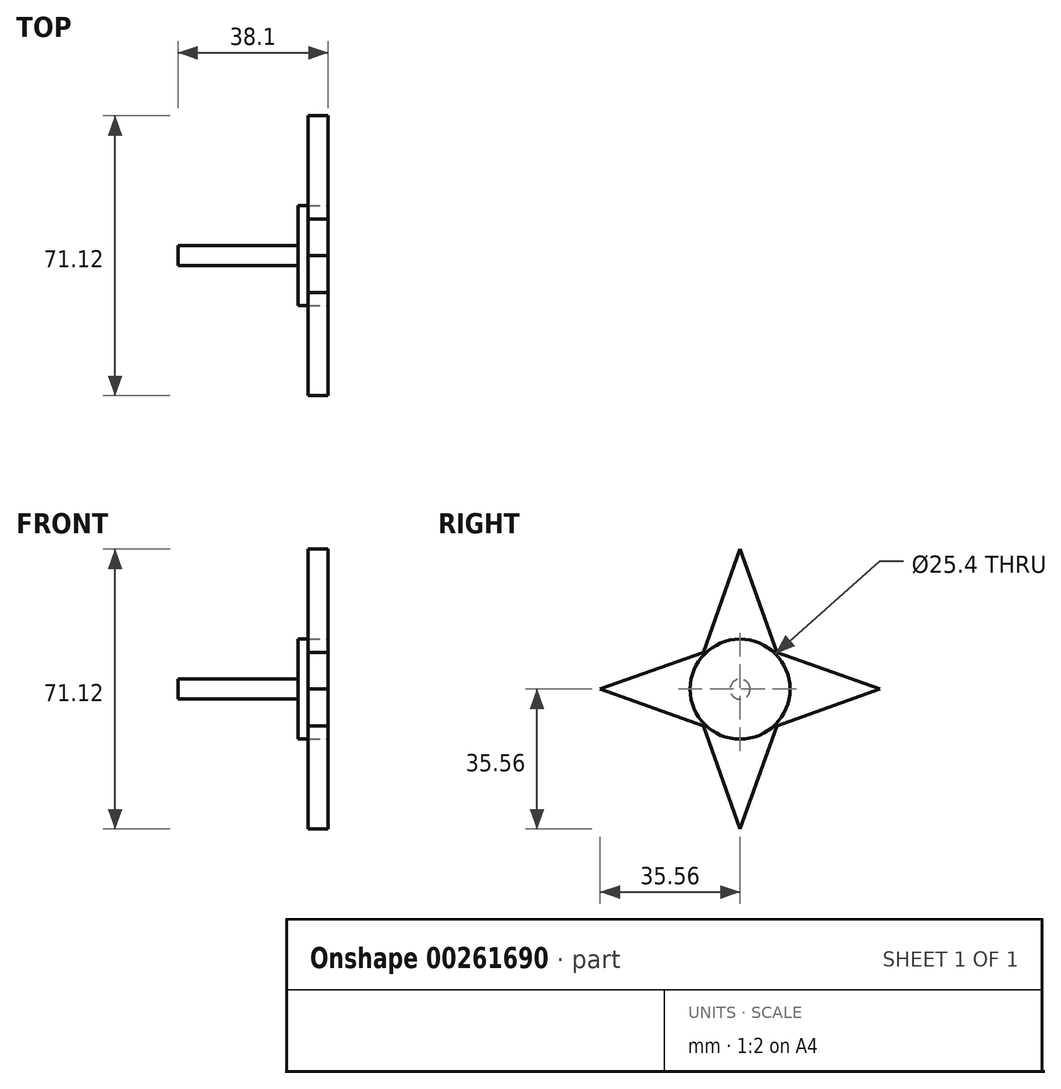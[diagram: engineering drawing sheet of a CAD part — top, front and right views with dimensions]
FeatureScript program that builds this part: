
annotation { "Feature Type Name" : "Feature", "Feature Type Description" : "" }
export const myFeature = defineFeature(function(context is Context, id is Id, definition is map)
    precondition{}
    {
        {
            var Q0;
            Q0=qCreatedBy(makeId("Right.planeOp"),FACE);
            var sketch = newSketch(context, id + "F0", { "sketchPlane" : qUnion([Q0])});
            skLineSegment(sketch, "E0.bottom", {"start": v(0, 0) * mm, "end": v(-71.12, 0) * mm});
            skLineSegment(sketch, "E0.top", {"start": v(0, -71.12) * mm, "end": v(-71.12, -71.12) * mm});
            skLineSegment(sketch, "E0.left", {"start": v(0, 0) * mm, "end": v(0, -71.12) * mm});
            skLineSegment(sketch, "E0.right", {"start": v(-71.12, 0) * mm, "end": v(-71.12, -71.12) * mm});
            skLineSegment(sketch, "E1", {"start": v(-35.56, 0) * mm, "end": v(-35.56, -71.12) * mm});
            skLineSegment(sketch, "E2", {"start": v(0, -35.56) * mm, "end": v(-71.12, -35.56) * mm});
            skLineSegment(sketch, "E3", {"start": v(-35.56, 0) * mm, "end": v(-22.86, -35.56) * mm});
            skLineSegment(sketch, "E4", {"start": v(0, -35.56) * mm, "end": v(-35.56, -22.86) * mm});
            skLineSegment(sketch, "E5", {"start": v(0, -35.56) * mm, "end": v(-35.56, -48.26) * mm});
            skLineSegment(sketch, "E6", {"start": v(-22.86, -35.56) * mm, "end": v(-35.56, -71.12) * mm});
            skLineSegment(sketch, "E7", {"start": v(-35.56, -71.12) * mm, "end": v(-48.26, -35.56) * mm});
            skLineSegment(sketch, "E8", {"start": v(-48.26, -35.56) * mm, "end": v(-35.56, 0) * mm});
            skLineSegment(sketch, "E9", {"start": v(-35.56, -22.86) * mm, "end": v(-71.12, -35.56) * mm});
            skLineSegment(sketch, "E10", {"start": v(-71.12, -35.56) * mm, "end": v(-35.56, -48.26) * mm});
            skCircle(sketch, "E11", {"center": v(-35.56, -35.56) * mm, "radius": 2.54 * mm});
            skCircle(sketch, "E12", {"center": v(-35.56, -35.56) * mm, "radius": 12.7 * mm});
            skSolve(sketch);
        }
        {
            var Q0;
            {var subQ0=sQuery(id+"F0.wireOp",EDGE,"E2");var subQ1=sQuery(id+"F0.wireOp",EDGE,"E1");var subQ2=makeQuery(id+"F0.imprint","INTERSECT",VERTEX,{"derivedFrom":[subQ1,subQ0]});Q0=makeQuery(id+"F0.imprint","IMPRINT",FACE,{"disambiguationData":[TD([[makeQuery(id+"F0.imprint","IMPRINT",EDGE,{"disambiguationData":[TD([[subQ2,-1.0]])],"derivedFrom":subQ1}),-1.0]])]});}
            var Q1;
            {var subQ0=sQuery(id+"F0.wireOp",EDGE,"E11");var subQ1=sQuery(id+"F0.wireOp",EDGE,"E1");var subQ2=makeQuery(id+"F0.imprint","INTERSECT",VERTEX,{"disambiguationData":[OD(0.0)],"derivedFrom":[subQ1,subQ0]});Q1=makeQuery(id+"F0.imprint","IMPRINT",FACE,{"disambiguationData":[TD([[makeQuery(id+"F0.imprint","IMPRINT",EDGE,{"disambiguationData":[TD([[subQ2,-1.0]])],"derivedFrom":subQ1}),-1.0]])]});}
            var Q2;
            {var subQ0=sQuery(id+"F0.wireOp",EDGE,"E11");var subQ1=sQuery(id+"F0.wireOp",EDGE,"E1");var subQ2=makeQuery(id+"F0.imprint","INTERSECT",VERTEX,{"disambiguationData":[OD(0.0)],"derivedFrom":[subQ1,subQ0]});Q2=makeQuery(id+"F0.imprint","IMPRINT",FACE,{"disambiguationData":[TD([[makeQuery(id+"F0.imprint","IMPRINT",EDGE,{"disambiguationData":[TD([[subQ2,-1.0]])],"derivedFrom":subQ1}),1.0]])]});}
            var Q3;
            {var subQ0=sQuery(id+"F0.wireOp",EDGE,"E2");var subQ1=sQuery(id+"F0.wireOp",EDGE,"E1");var subQ2=makeQuery(id+"F0.imprint","INTERSECT",VERTEX,{"derivedFrom":[subQ1,subQ0]});Q3=makeQuery(id+"F0.imprint","IMPRINT",FACE,{"disambiguationData":[TD([[makeQuery(id+"F0.imprint","IMPRINT",EDGE,{"disambiguationData":[TD([[subQ2,-1.0]])],"derivedFrom":subQ1}),1.0]])]});}
            extrude(context, id + "F1", {"entities" : qUnion([Q0, Q1, Q2, Q3]), "oppositeDirection" : true, "depth" : 38.1 * mm});
        }
        {
            var Q0;
            {var subQ1=sQuery(id+"F0.wireOp",EDGE,"E1");var subQ7=sQuery(id+"F0.wireOp",EDGE,"E11");var subQ9=makeQuery(id+"F0.imprint","INTERSECT",VERTEX,{"disambiguationData":[OD(0.0)],"derivedFrom":[subQ1,subQ7]});Q0=makeQuery(id+"F0.imprint","IMPRINT",FACE,{"disambiguationData":[TD([[makeQuery(id+"F0.imprint","IMPRINT",EDGE,{"disambiguationData":[TD([[subQ9,1.0]])],"derivedFrom":subQ7}),-1.0]])]});}
            var Q1;
            {var subQ1=sQuery(id+"F0.wireOp",EDGE,"E1");var subQ7=sQuery(id+"F0.wireOp",EDGE,"E11");var subQ9=makeQuery(id+"F0.imprint","INTERSECT",VERTEX,{"disambiguationData":[OD(0.0)],"derivedFrom":[subQ1,subQ7]});Q1=makeQuery(id+"F0.imprint","IMPRINT",FACE,{"disambiguationData":[TD([[makeQuery(id+"F0.imprint","IMPRINT",EDGE,{"disambiguationData":[TD([[subQ9,-1.0]])],"derivedFrom":subQ7}),-1.0]])]});}
            var Q2;
            {var subQ1=sQuery(id+"F0.wireOp",EDGE,"E1");var subQ7=sQuery(id+"F0.wireOp",EDGE,"E11");var subQ9=makeQuery(id+"F0.imprint","INTERSECT",VERTEX,{"disambiguationData":[OD(1.0)],"derivedFrom":[subQ1,subQ7]});Q2=makeQuery(id+"F0.imprint","IMPRINT",FACE,{"disambiguationData":[TD([[makeQuery(id+"F0.imprint","IMPRINT",EDGE,{"disambiguationData":[TD([[subQ9,1.0]])],"derivedFrom":subQ7}),-1.0]])]});}
            var Q3;
            {var subQ5=sQuery(id+"F0.wireOp",EDGE,"E11");var subQ7=sQuery(id+"F0.wireOp",EDGE,"E1");var subQ9=makeQuery(id+"F0.imprint","INTERSECT",VERTEX,{"disambiguationData":[OD(1.0)],"derivedFrom":[subQ7,subQ5]});Q3=makeQuery(id+"F0.imprint","IMPRINT",FACE,{"disambiguationData":[TD([[makeQuery(id+"F0.imprint","IMPRINT",EDGE,{"disambiguationData":[TD([[subQ9,-1.0]])],"derivedFrom":subQ5}),-1.0]])]});}
            var Q4;
            {var subQ0=sQuery(id+"F0.wireOp",EDGE,"E12");var subQ1=sQuery(id+"F0.wireOp",EDGE,"E8");var subQ3=makeQuery(id+"F0.imprint","INTERSECT",VERTEX,{"derivedFrom":[subQ1,subQ0]});Q4=makeQuery(id+"F0.imprint","IMPRINT",FACE,{"disambiguationData":[TD([[makeQuery(id+"F0.imprint","IMPRINT",EDGE,{"disambiguationData":[TD([[subQ3,1.0]])],"derivedFrom":subQ1}),1.0]])]});}
            var Q5;
            {var subQ0=sQuery(id+"F0.wireOp",EDGE,"E12");var subQ1=sQuery(id+"F0.wireOp",EDGE,"E9");var subQ3=makeQuery(id+"F0.imprint","INTERSECT",VERTEX,{"derivedFrom":[subQ1,subQ0]});Q5=makeQuery(id+"F0.imprint","IMPRINT",FACE,{"disambiguationData":[TD([[makeQuery(id+"F0.imprint","IMPRINT",EDGE,{"disambiguationData":[TD([[subQ3,1.0]])],"derivedFrom":subQ1}),-1.0]])]});}
            var Q6;
            {var subQ0=sQuery(id+"F0.wireOp",EDGE,"E12");var subQ1=sQuery(id+"F0.wireOp",EDGE,"E4");var subQ3=makeQuery(id+"F0.imprint","INTERSECT",VERTEX,{"derivedFrom":[subQ1,subQ0]});Q6=makeQuery(id+"F0.imprint","IMPRINT",FACE,{"disambiguationData":[TD([[makeQuery(id+"F0.imprint","IMPRINT",EDGE,{"disambiguationData":[TD([[subQ3,-1.0]])],"derivedFrom":subQ1}),-1.0]])]});}
            var Q7;
            {var subQ0=sQuery(id+"F0.wireOp",EDGE,"E12");var subQ1=sQuery(id+"F0.wireOp",EDGE,"E3");var subQ3=makeQuery(id+"F0.imprint","INTERSECT",VERTEX,{"derivedFrom":[subQ1,subQ0]});Q7=makeQuery(id+"F0.imprint","IMPRINT",FACE,{"disambiguationData":[TD([[makeQuery(id+"F0.imprint","IMPRINT",EDGE,{"disambiguationData":[TD([[subQ3,-1.0]])],"derivedFrom":subQ1}),1.0]])]});}
            var Q8;
            {var subQ0=sQuery(id+"F0.wireOp",EDGE,"E12");var subQ1=sQuery(id+"F0.wireOp",EDGE,"E6");var subQ3=makeQuery(id+"F0.imprint","INTERSECT",VERTEX,{"derivedFrom":[subQ1,subQ0]});Q8=makeQuery(id+"F0.imprint","IMPRINT",FACE,{"disambiguationData":[TD([[makeQuery(id+"F0.imprint","IMPRINT",EDGE,{"disambiguationData":[TD([[subQ3,1.0]])],"derivedFrom":subQ1}),1.0]])]});}
            var Q9;
            {var subQ0=sQuery(id+"F0.wireOp",EDGE,"E12");var subQ1=sQuery(id+"F0.wireOp",EDGE,"E5");var subQ3=makeQuery(id+"F0.imprint","INTERSECT",VERTEX,{"derivedFrom":[subQ1,subQ0]});Q9=makeQuery(id+"F0.imprint","IMPRINT",FACE,{"disambiguationData":[TD([[makeQuery(id+"F0.imprint","IMPRINT",EDGE,{"disambiguationData":[TD([[subQ3,-1.0]])],"derivedFrom":subQ1}),1.0]])]});}
            var Q10;
            {var subQ0=sQuery(id+"F0.wireOp",EDGE,"E12");var subQ1=sQuery(id+"F0.wireOp",EDGE,"E10");var subQ3=makeQuery(id+"F0.imprint","INTERSECT",VERTEX,{"derivedFrom":[subQ1,subQ0]});Q10=makeQuery(id+"F0.imprint","IMPRINT",FACE,{"disambiguationData":[TD([[makeQuery(id+"F0.imprint","IMPRINT",EDGE,{"disambiguationData":[TD([[subQ3,-1.0]])],"derivedFrom":subQ1}),-1.0]])]});}
            var Q11;
            {var subQ0=sQuery(id+"F0.wireOp",EDGE,"E12");var subQ1=sQuery(id+"F0.wireOp",EDGE,"E7");var subQ3=makeQuery(id+"F0.imprint","INTERSECT",VERTEX,{"derivedFrom":[subQ1,subQ0]});Q11=makeQuery(id+"F0.imprint","IMPRINT",FACE,{"disambiguationData":[TD([[makeQuery(id+"F0.imprint","IMPRINT",EDGE,{"disambiguationData":[TD([[subQ3,-1.0]])],"derivedFrom":subQ1}),1.0]])]});}
            extrude(context, id + "F2", {"entities" : qUnion([Q0, Q1, Q2, Q3, Q4, Q5, Q6, Q7, Q8, Q9, Q10, Q11]), "operationType" : NewBodyOperationType.ADD, "oppositeDirection" : true, "depth" : 7.62 * mm});
        }
        {
            var Q0;
            {var subQ3=sQuery(id+"F0.wireOp",EDGE,"E12");var subQ4=sQuery(id+"F0.wireOp",EDGE,"E8");var subQ6=makeQuery(id+"F0.imprint","INTERSECT",VERTEX,{"derivedFrom":[subQ4,subQ3]});Q0=makeQuery(id+"F0.imprint","IMPRINT",FACE,{"disambiguationData":[TD([[makeQuery(id+"F0.imprint","IMPRINT",EDGE,{"disambiguationData":[TD([[subQ6,-1.0]])],"derivedFrom":subQ4}),1.0]])]});}
            var Q1;
            {var subQ0=sQuery(id+"F0.wireOp",EDGE,"E10");var subQ4=sQuery(id+"F0.wireOp",EDGE,"E7");var subQ7=makeQuery(id+"F0.imprint","INTERSECT",VERTEX,{"derivedFrom":[subQ4,subQ0]});Q1=makeQuery(id+"F0.imprint","IMPRINT",FACE,{"disambiguationData":[TD([[makeQuery(id+"F0.imprint","IMPRINT",EDGE,{"disambiguationData":[TD([[subQ7,-1.0]])],"derivedFrom":subQ4}),1.0]])]});}
            var Q2;
            {var subQ0=sQuery(id+"F0.wireOp",EDGE,"E7");var subQ4=sQuery(id+"F0.wireOp",EDGE,"E10");var subQ6=makeQuery(id+"F0.imprint","INTERSECT",VERTEX,{"derivedFrom":[subQ0,subQ4]});Q2=makeQuery(id+"F0.imprint","IMPRINT",FACE,{"disambiguationData":[TD([[makeQuery(id+"F0.imprint","IMPRINT",EDGE,{"disambiguationData":[TD([[subQ6,-1.0]])],"derivedFrom":subQ4}),-1.0]])]});}
            var Q3;
            {var subQ0=sQuery(id+"F0.wireOp",EDGE,"E6");var subQ4=sQuery(id+"F0.wireOp",EDGE,"E5");var subQ6=makeQuery(id+"F0.imprint","INTERSECT",VERTEX,{"derivedFrom":[subQ4,subQ0]});Q3=makeQuery(id+"F0.imprint","IMPRINT",FACE,{"disambiguationData":[TD([[makeQuery(id+"F0.imprint","IMPRINT",EDGE,{"disambiguationData":[TD([[subQ6,-1.0]])],"derivedFrom":subQ4}),1.0]])]});}
            var Q4;
            {var subQ0=sQuery(id+"F0.wireOp",EDGE,"E5");var subQ4=sQuery(id+"F0.wireOp",EDGE,"E6");var subQ7=makeQuery(id+"F0.imprint","INTERSECT",VERTEX,{"derivedFrom":[subQ0,subQ4]});Q4=makeQuery(id+"F0.imprint","IMPRINT",FACE,{"disambiguationData":[TD([[makeQuery(id+"F0.imprint","IMPRINT",EDGE,{"disambiguationData":[TD([[subQ7,1.0]])],"derivedFrom":subQ4}),1.0]])]});}
            var Q5;
            {var subQ0=sQuery(id+"F0.wireOp",EDGE,"E4");var subQ4=sQuery(id+"F0.wireOp",EDGE,"E3");var subQ6=makeQuery(id+"F0.imprint","INTERSECT",VERTEX,{"derivedFrom":[subQ4,subQ0]});Q5=makeQuery(id+"F0.imprint","IMPRINT",FACE,{"disambiguationData":[TD([[makeQuery(id+"F0.imprint","IMPRINT",EDGE,{"disambiguationData":[TD([[subQ6,-1.0]])],"derivedFrom":subQ4}),1.0]])]});}
            var Q6;
            {var subQ0=sQuery(id+"F0.wireOp",EDGE,"E3");var subQ4=sQuery(id+"F0.wireOp",EDGE,"E4");var subQ6=makeQuery(id+"F0.imprint","INTERSECT",VERTEX,{"derivedFrom":[subQ0,subQ4]});Q6=makeQuery(id+"F0.imprint","IMPRINT",FACE,{"disambiguationData":[TD([[makeQuery(id+"F0.imprint","IMPRINT",EDGE,{"disambiguationData":[TD([[subQ6,-1.0]])],"derivedFrom":subQ4}),-1.0]])]});}
            var Q7;
            {var subQ0=sQuery(id+"F0.wireOp",EDGE,"E8");var subQ4=sQuery(id+"F0.wireOp",EDGE,"E9");var subQ6=makeQuery(id+"F0.imprint","INTERSECT",VERTEX,{"derivedFrom":[subQ0,subQ4]});Q7=makeQuery(id+"F0.imprint","IMPRINT",FACE,{"disambiguationData":[TD([[makeQuery(id+"F0.imprint","IMPRINT",EDGE,{"disambiguationData":[TD([[subQ6,1.0]])],"derivedFrom":subQ4}),-1.0]])]});}
            var Q8;
            {var subQ0=sQuery(id+"F0.wireOp",EDGE,"E12");var subQ1=sQuery(id+"F0.wireOp",EDGE,"E8");var subQ2=makeQuery(id+"F0.imprint","INTERSECT",VERTEX,{"derivedFrom":[subQ1,subQ0]});Q8=makeQuery(id+"F0.imprint","IMPRINT",FACE,{"disambiguationData":[TD([[makeQuery(id+"F0.imprint","IMPRINT",EDGE,{"disambiguationData":[TD([[subQ2,-1.0]])],"derivedFrom":subQ1}),-1.0]])]});}
            var Q9;
            {var subQ0=sQuery(id+"F0.wireOp",EDGE,"E10");var subQ1=sQuery(id+"F0.wireOp",EDGE,"E7");var subQ2=makeQuery(id+"F0.imprint","INTERSECT",VERTEX,{"derivedFrom":[subQ1,subQ0]});Q9=makeQuery(id+"F0.imprint","IMPRINT",FACE,{"disambiguationData":[TD([[makeQuery(id+"F0.imprint","IMPRINT",EDGE,{"disambiguationData":[TD([[subQ2,-1.0]])],"derivedFrom":subQ1}),-1.0]])]});}
            var Q10;
            {var subQ0=sQuery(id+"F0.wireOp",EDGE,"E6");var subQ1=sQuery(id+"F0.wireOp",EDGE,"E5");var subQ2=makeQuery(id+"F0.imprint","INTERSECT",VERTEX,{"derivedFrom":[subQ1,subQ0]});Q10=makeQuery(id+"F0.imprint","IMPRINT",FACE,{"disambiguationData":[TD([[makeQuery(id+"F0.imprint","IMPRINT",EDGE,{"disambiguationData":[TD([[subQ2,-1.0]])],"derivedFrom":subQ1}),-1.0]])]});}
            var Q11;
            {var subQ0=sQuery(id+"F0.wireOp",EDGE,"E4");var subQ1=sQuery(id+"F0.wireOp",EDGE,"E3");var subQ2=makeQuery(id+"F0.imprint","INTERSECT",VERTEX,{"derivedFrom":[subQ1,subQ0]});Q11=makeQuery(id+"F0.imprint","IMPRINT",FACE,{"disambiguationData":[TD([[makeQuery(id+"F0.imprint","IMPRINT",EDGE,{"disambiguationData":[TD([[subQ2,-1.0]])],"derivedFrom":subQ1}),-1.0]])]});}
            extrude(context, id + "F3", {"entities" : qUnion([Q0, Q1, Q2, Q3, Q4, Q5, Q6, Q7, Q8, Q9, Q10, Q11]), "oppositeDirection" : true, "depth" : 5.08 * mm});
        }
    });
